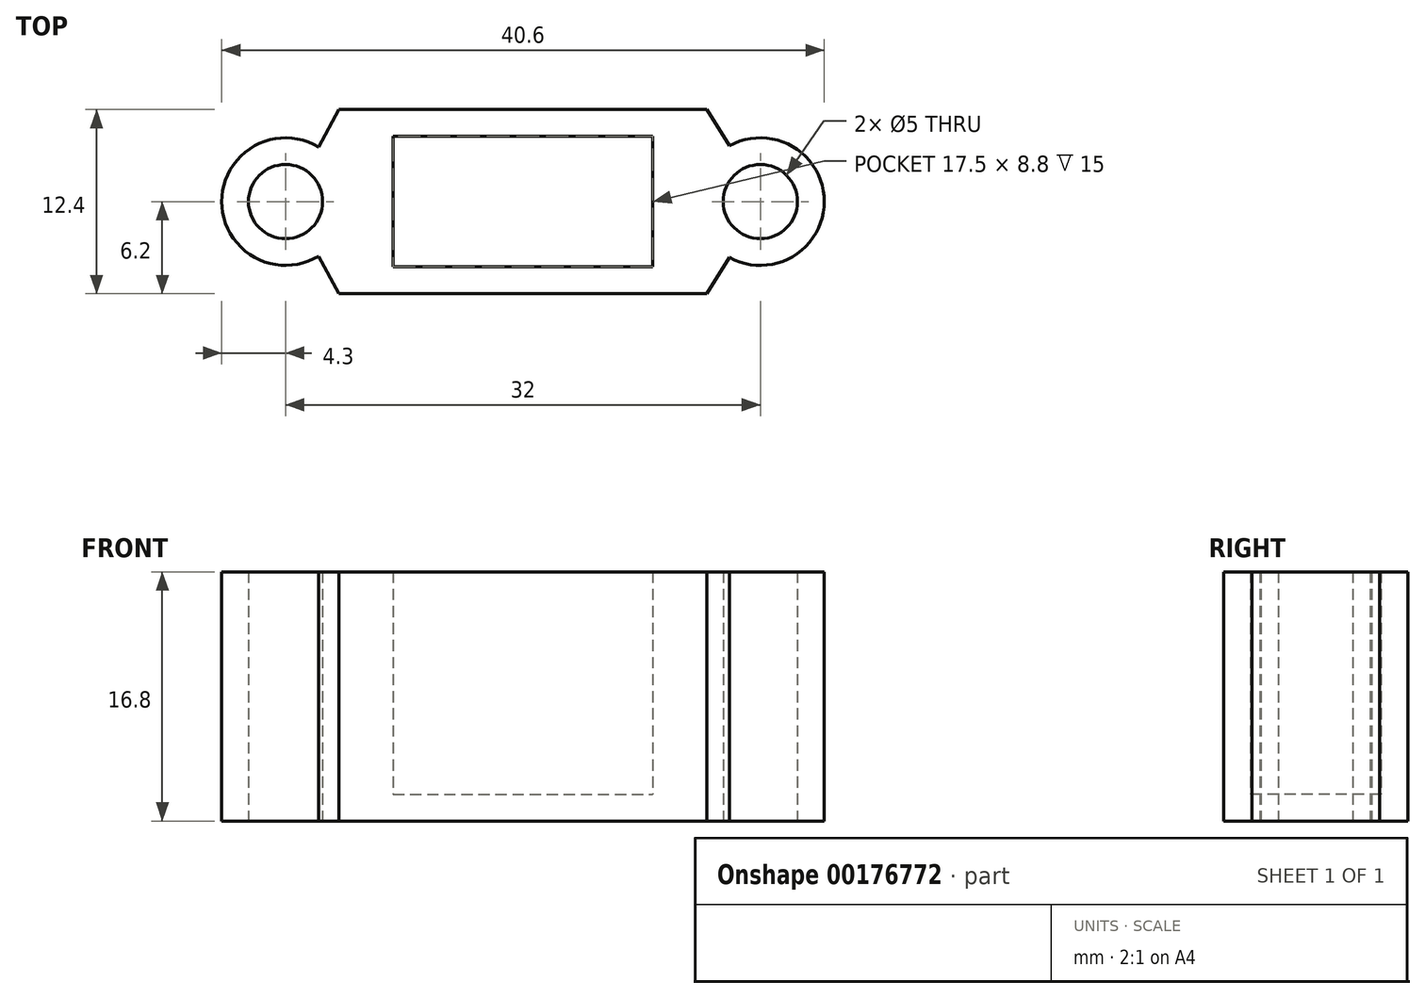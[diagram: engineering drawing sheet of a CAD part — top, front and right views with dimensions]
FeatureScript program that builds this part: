
annotation { "Feature Type Name" : "Feature", "Feature Type Description" : "" }
export const myFeature = defineFeature(function(context is Context, id is Id, definition is map)
    precondition{}
    {
        {
            assignVariable(context, id + "F0", {"name" : "pieceHeight", "anyValue" : 15});
        }
        {
            assignVariable(context, id + "F1", {"name" : "thickness", "anyValue" : 1.8});
        }
        {
            var Q0;
            Q0=qCreatedBy(makeId("Top.planeOp"),FACE);
            var sketch = newSketch(context, id + "F2", { "sketchPlane" : qUnion([Q0])});
            skCircle(sketch, "E0", {"center": v(-16, 0) * mm, "radius": 2.5 * mm});
            skCircle(sketch, "E1", {"center": v(16, 0) * mm, "radius": 2.5 * mm});
            skCircle(sketch, "E2.0", {"center": v(-16, 0) * mm, "radius": 4.3 * mm});
            skCircle(sketch, "E3.0", {"center": v(16, 0) * mm, "radius": 4.3 * mm});
            skLineSegment(sketch, "E4", {"start": v(-16, 0) * mm, "end": v(16, 0) * mm, "construction": true});
            skLineSegment(sketch, "E5.bottom", {"start": v(-8.75, 4.4) * mm, "end": v(8.75, 4.4) * mm});
            skLineSegment(sketch, "E5.top", {"start": v(-8.75, -4.4) * mm, "end": v(8.75, -4.4) * mm});
            skLineSegment(sketch, "E5.left", {"start": v(-8.75, 4.4) * mm, "end": v(-8.75, -4.4) * mm});
            skLineSegment(sketch, "E5.right", {"start": v(8.75, 4.4) * mm, "end": v(8.75, -4.4) * mm});
            skPoint(sketch, "E5.middle", {"position": v(0, 0) * mm});
            skLineSegment(sketch, "E6", {"start": v(-13.77, 3.68) * mm, "end": v(-12.4, 6.2) * mm});
            skLineSegment(sketch, "E7", {"start": v(-12.4, 6.2) * mm, "end": v(0, 6.2) * mm});
            skLineSegment(sketch, "E8", {"start": v(0, 6.2) * mm, "end": v(12.4, 6.2) * mm});
            skLineSegment(sketch, "E9", {"start": v(12.4, 6.2) * mm, "end": v(13.91, 3.76) * mm});
            skLineSegment(sketch, "E10.MirrorCS", {"start": v(0, -6.2) * mm, "end": v(12.4, -6.2) * mm});
            skLineSegment(sketch, "E11.MirrorCS", {"start": v(12.4, -6.2) * mm, "end": v(13.91, -3.76) * mm});
            skLineSegment(sketch, "E12.MirrorCS", {"start": v(-12.4, -6.2) * mm, "end": v(0, -6.2) * mm});
            skLineSegment(sketch, "E13.MirrorCS", {"start": v(-13.77, -3.68) * mm, "end": v(-12.4, -6.2) * mm});
            skSolve(sketch);
        }
        {
            var Q0;
            Q0=qSketchRegion(id+"F2",true);
            extrude(context, id + "F3", {"entities" : qUnion([Q0]), "depth" : (getVariable(context, 'pieceHeight')) * mm});
        }
        {
            var Q0;
            Q0=makeQuery(id+"F3.opExtrude","CAP_FACE",FACE,{"disambiguationData":[OSD([sQuery(id+"F2.wireOp",EDGE,"E0"),sQuery(id+"F2.wireOp",EDGE,"E1"),sQuery(id+"F2.wireOp",EDGE,"E2.0"),sQuery(id+"F2.wireOp",EDGE,"E3.0"),sQuery(id+"F2.wireOp",EDGE,"E5.bottom"),sQuery(id+"F2.wireOp",EDGE,"E5.top"),sQuery(id+"F2.wireOp",EDGE,"E5.left"),sQuery(id+"F2.wireOp",EDGE,"E5.right"),sQuery(id+"F2.wireOp",EDGE,"E6"),sQuery(id+"F2.wireOp",EDGE,"E7"),sQuery(id+"F2.wireOp",EDGE,"E8"),sQuery(id+"F2.wireOp",EDGE,"E9"),sQuery(id+"F2.wireOp",EDGE,"E10.MirrorCS"),sQuery(id+"F2.wireOp",EDGE,"E11.MirrorCS"),sQuery(id+"F2.wireOp",EDGE,"E12.MirrorCS"),sQuery(id+"F2.wireOp",EDGE,"E13.MirrorCS")])],"isStart":true});
            var sketch = newSketch(context, id + "F4", { "sketchPlane" : qUnion([Q0])});
            skLineSegment(sketch, "E14.bottom", {"start": v(-8.75, 4.4) * mm, "end": v(8.75, 4.4) * mm});
            skLineSegment(sketch, "E14.top", {"start": v(-8.75, -4.4) * mm, "end": v(8.75, -4.4) * mm});
            skLineSegment(sketch, "E14.left", {"start": v(-8.75, 4.4) * mm, "end": v(-8.75, -4.4) * mm});
            skLineSegment(sketch, "E14.right", {"start": v(8.75, 4.4) * mm, "end": v(8.75, -4.4) * mm});
            skPoint(sketch, "E14.middle", {"position": v(0, 0) * mm});
            skSolve(sketch);
        }
        {
            var Q0;
            Q0 = qSketchRegion(id + "F4", true);
            var Q1;
            Q1=makeQuery(id+"F4.imprint","IMPRINT",FACE,{"disambiguationData":[TD([[makeQuery(id+"F4.imprint","IMPRINT",EDGE,{"derivedFrom":sQuery(id+"F4.wireOp",EDGE,"E14.bottom")}),1.0]])]});
            extrude(context, id + "F5", {"entities" : qUnion([Q0, Q1]), "operationType" : NewBodyOperationType.ADD, "depth" : (getVariable(context, 'thickness')) * mm});
        }
    });
